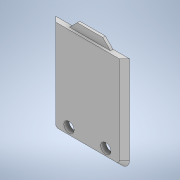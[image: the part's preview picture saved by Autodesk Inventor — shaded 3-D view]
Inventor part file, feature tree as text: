
AUTODESK INVENTOR PART (.ipt)
format: ipt  version: 2021.1 (Build 251245010, 245A)  size: 139,776 bytes
history: native  units: mm
features: extrude x2, sketch x2, chamfer x1, projected_geometry x1
ambient origin geometry x8: Origin, YZ Plane, XZ Plane, XY Plane, X Axis, Y Axis, Z Axis, Center Point
bodies: Volumenkörper1 (feature_tree)
feature tree (6):
  extrude  "Extrusion1"  Depth=2.0mm TaperAngle=45.0deg
  chamfer  "Fase1"  Distance=1.0mm
  extrude  "Extrusion2"  [1 undecoded]
  sketch  "Skizze1"  dims[d0=2.0mm d1=0.0mm d2=2.0mm d3=2.0mm d4=45.0deg d5=1.0mm d6=0.0mm]
  sketch  "Skizze2"
  projected_geometry  "Projizierte Kontur1"
note: 1 required parameter value undecoded (feature->parameter linkage not recoverable at this tier; creation-order binding heuristic only, values carry confidence <= 0.55)
